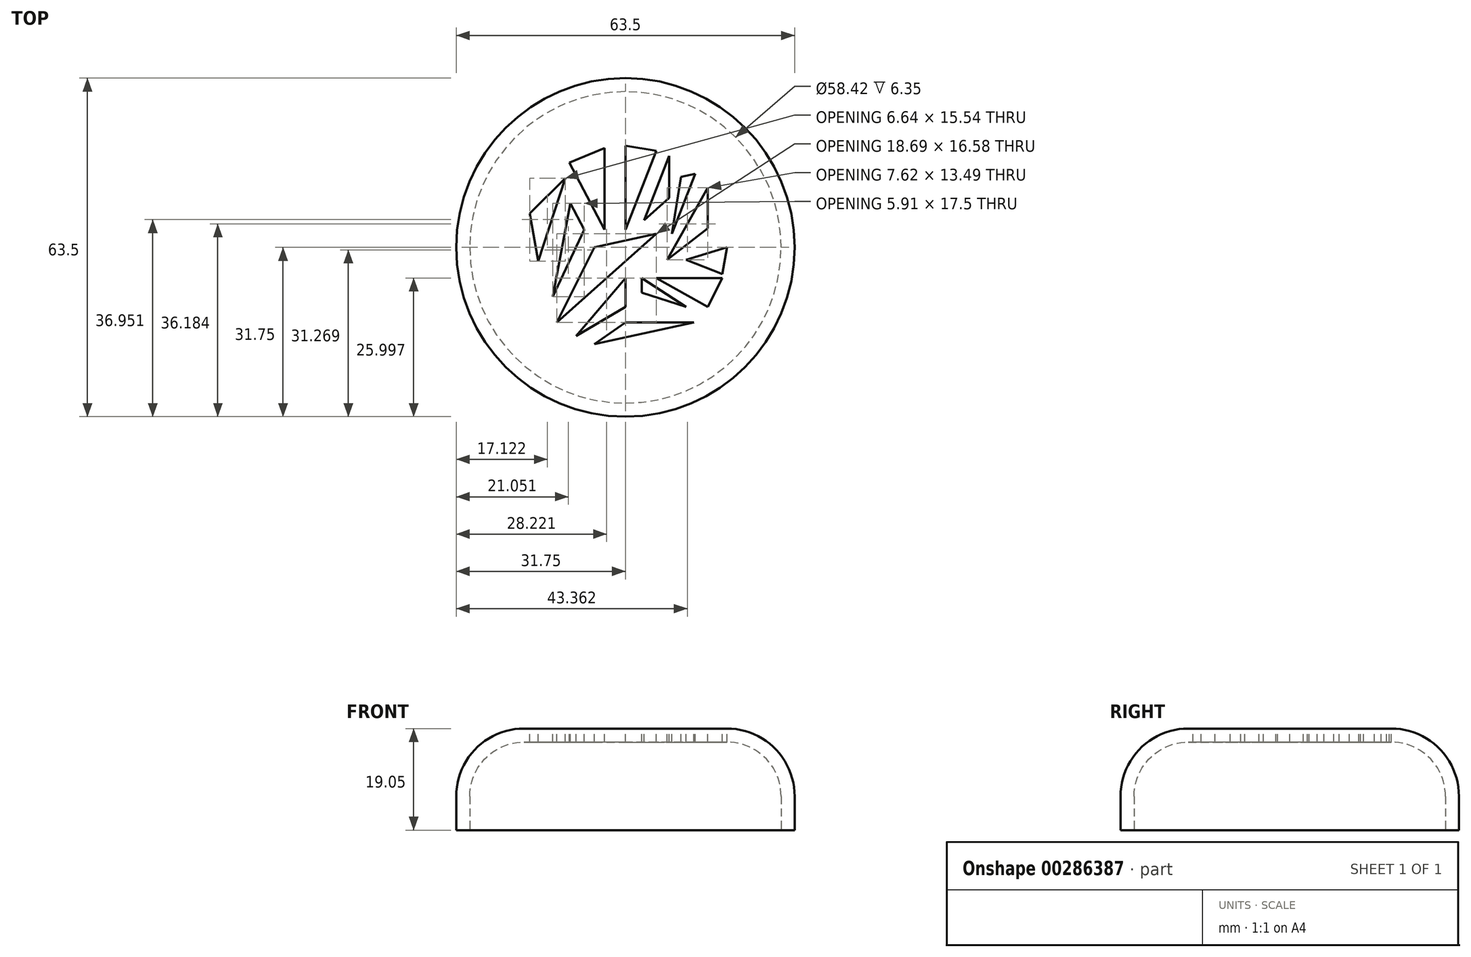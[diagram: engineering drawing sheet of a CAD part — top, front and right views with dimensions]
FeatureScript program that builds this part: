
annotation { "Feature Type Name" : "Feature", "Feature Type Description" : "" }
export const myFeature = defineFeature(function(context is Context, id is Id, definition is map)
    precondition{}
    {
        {
            var Q0;
            Q0=qCreatedBy(makeId("Top.planeOp"),FACE);
            var sketch = newSketch(context, id + "F0", { "sketchPlane" : qUnion([Q0])});
            skCircle(sketch, "E0", {"center": v(0, 0) * mm, "radius": 31.75 * mm});
            skSolve(sketch);
        }
        {
            var Q0;
            Q0 = qSketchRegion(id + "F0", true);
            extrude(context, id + "F1", {"entities" : qUnion([Q0]), "depth" : 19.05 * mm});
        }
        {
            var Q0;
            Q0=makeQuery(id+"F1.opExtrude","CAP_EDGE",EDGE,{"disambiguationData":[OSD([sQuery(id+"F0.wireOp",EDGE,"E0")])],"isStart":false});
            fillet(context, id + "F2", {"entities" : qUnion([Q0]), "radius" : 12.7 * mm, "tangentPropagation" : true, "allowEdgeOverflow" : false});
        }
        {
            var Q0;
            Q0=makeQuery(id+"F1.opExtrude","CAP_FACE",FACE,{"disambiguationData":[OSD([sQuery(id+"F0.wireOp",EDGE,"E0")])],"isStart":true});
            shell(context, id + "F3", {"entities" : qUnion([Q0]), "thickness" : 2.54 * mm});
        }
        {
            var Q0;
            Q0=makeQuery(id+"F1.opExtrude","CAP_FACE",FACE,{"disambiguationData":[OSD([sQuery(id+"F0.wireOp",EDGE,"E0")])],"isStart":false});
            var sketch = newSketch(context, id + "F4", { "sketchPlane" : qUnion([Q0])});
            skLineSegment(sketch, "E1", {"start": v(-3.92, 18.64) * mm, "end": v(-3.92, 3.3) * mm});
            skLineSegment(sketch, "E2", {"start": v(-3.92, 3.3) * mm, "end": v(-10.53, 15.88) * mm});
            skLineSegment(sketch, "E3", {"start": v(-10.53, 15.88) * mm, "end": v(-3.92, 18.64) * mm});
            skLineSegment(sketch, "E4", {"start": v(-12.87, -14.04) * mm, "end": v(-5.81, 0) * mm});
            skLineSegment(sketch, "E5", {"start": v(-5.81, 0) * mm, "end": v(5.81, 2.54) * mm});
            skLineSegment(sketch, "E6", {"start": v(5.81, 2.54) * mm, "end": v(-12.87, -14.04) * mm});
            skPoint(sketch, "E7.startSnap0", {"position": v(-3.53, -5.75) * mm});
            skLineSegment(sketch, "E8", {"start": v(12.87, -14.04) * mm, "end": v(-5.85, -18.13) * mm});
            skLineSegment(sketch, "E9", {"start": v(15.42, -11.18) * mm, "end": v(5.81, -5.75) * mm});
            skPoint(sketch, "E10", {"position": v(0, 1.27) * mm});
            skLineSegment(sketch, "E11", {"start": v(0, 19.05) * mm, "end": v(0, 3.3) * mm});
            skLineSegment(sketch, "E12", {"start": v(0, 3.3) * mm, "end": v(5.81, 18.14) * mm});
            skLineSegment(sketch, "E13", {"start": v(5.81, 18.14) * mm, "end": v(0, 19.05) * mm});
            skLineSegment(sketch, "E14", {"start": v(3.51, 5.13) * mm, "end": v(8.23, 17.18) * mm});
            skPoint(sketch, "E14.startSnap0", {"position": v(3.51, -16.09) * mm});
            skLineSegment(sketch, "E15", {"start": v(8.23, 17.18) * mm, "end": v(8.23, 9.3) * mm});
            skLineSegment(sketch, "E16", {"start": v(8.23, 9.3) * mm, "end": v(3.51, 5.13) * mm});
            skLineSegment(sketch, "E17", {"start": v(10.45, 13.25) * mm, "end": v(13.1, 13.83) * mm});
            skLineSegment(sketch, "E18", {"start": v(13.1, 13.83) * mm, "end": v(8.68, 2.54) * mm});
            skLineSegment(sketch, "E19", {"start": v(8.68, 2.54) * mm, "end": v(10.45, 13.25) * mm});
            skLineSegment(sketch, "E20", {"start": v(-17.95, 6.4) * mm, "end": v(-11.31, 12.97) * mm});
            skLineSegment(sketch, "E21", {"start": v(-11.31, 12.97) * mm, "end": v(-16.37, -2.57) * mm});
            skLineSegment(sketch, "E22", {"start": v(-16.37, -2.57) * mm, "end": v(-17.95, 6.4) * mm});
            skLineSegment(sketch, "E23", {"start": v(-10.35, 8.27) * mm, "end": v(-7.75, 3.3) * mm});
            skLineSegment(sketch, "E24", {"start": v(-7.75, 3.3) * mm, "end": v(-13.65, -9.23) * mm});
            skLineSegment(sketch, "E25", {"start": v(-13.65, -9.23) * mm, "end": v(-10.35, 8.27) * mm});
            skLineSegment(sketch, "E26", {"start": v(12.87, -14.04) * mm, "end": v(0, -14.04) * mm});
            skLineSegment(sketch, "E27", {"start": v(0, -14.04) * mm, "end": v(-5.85, -18.13) * mm});
            skLineSegment(sketch, "E28", {"start": v(-9.27, -16.64) * mm, "end": v(0, -11.18) * mm});
            skLineSegment(sketch, "E29", {"start": v(0, -11.18) * mm, "end": v(0, -5.75) * mm});
            skLineSegment(sketch, "E30", {"start": v(0, -5.75) * mm, "end": v(-9.27, -16.64) * mm});
            skLineSegment(sketch, "E31", {"start": v(11.37, -11.18) * mm, "end": v(3.05, -5.75) * mm});
            skLineSegment(sketch, "E32", {"start": v(3.05, -5.75) * mm, "end": v(3.05, -8.47) * mm});
            skPoint(sketch, "E32.endSnap0", {"position": v(0, -8.47) * mm});
            skLineSegment(sketch, "E33", {"start": v(3.05, -8.47) * mm, "end": v(11.37, -11.18) * mm});
            skLineSegment(sketch, "E34", {"start": v(5.81, -5.75) * mm, "end": v(18.16, -5.75) * mm});
            skLineSegment(sketch, "E35", {"start": v(18.16, -5.75) * mm, "end": v(15.42, -11.18) * mm});
            skLineSegment(sketch, "E36", {"start": v(15.42, 11.18) * mm, "end": v(7.8, -2.31) * mm});
            skLineSegment(sketch, "E37", {"start": v(7.8, -2.31) * mm, "end": v(15.42, 3.6) * mm});
            skLineSegment(sketch, "E38", {"start": v(15.42, 3.6) * mm, "end": v(15.42, 11.18) * mm});
            skLineSegment(sketch, "E39", {"start": v(19.05, 0) * mm, "end": v(11.37, -2.31) * mm});
            skLineSegment(sketch, "E40", {"start": v(11.37, -2.31) * mm, "end": v(18.16, -4.97) * mm});
            skLineSegment(sketch, "E41", {"start": v(18.16, -4.97) * mm, "end": v(19.05, 0) * mm});
            skSolve(sketch);
        }
        {
            var Q0;
            Q0 = qSketchRegion(id + "F4", true);
            extrude(context, id + "F5", {"entities" : qUnion([Q0]), "operationType" : NewBodyOperationType.REMOVE, "oppositeDirection" : true, "depth" : 25.4 * mm});
        }
    });
